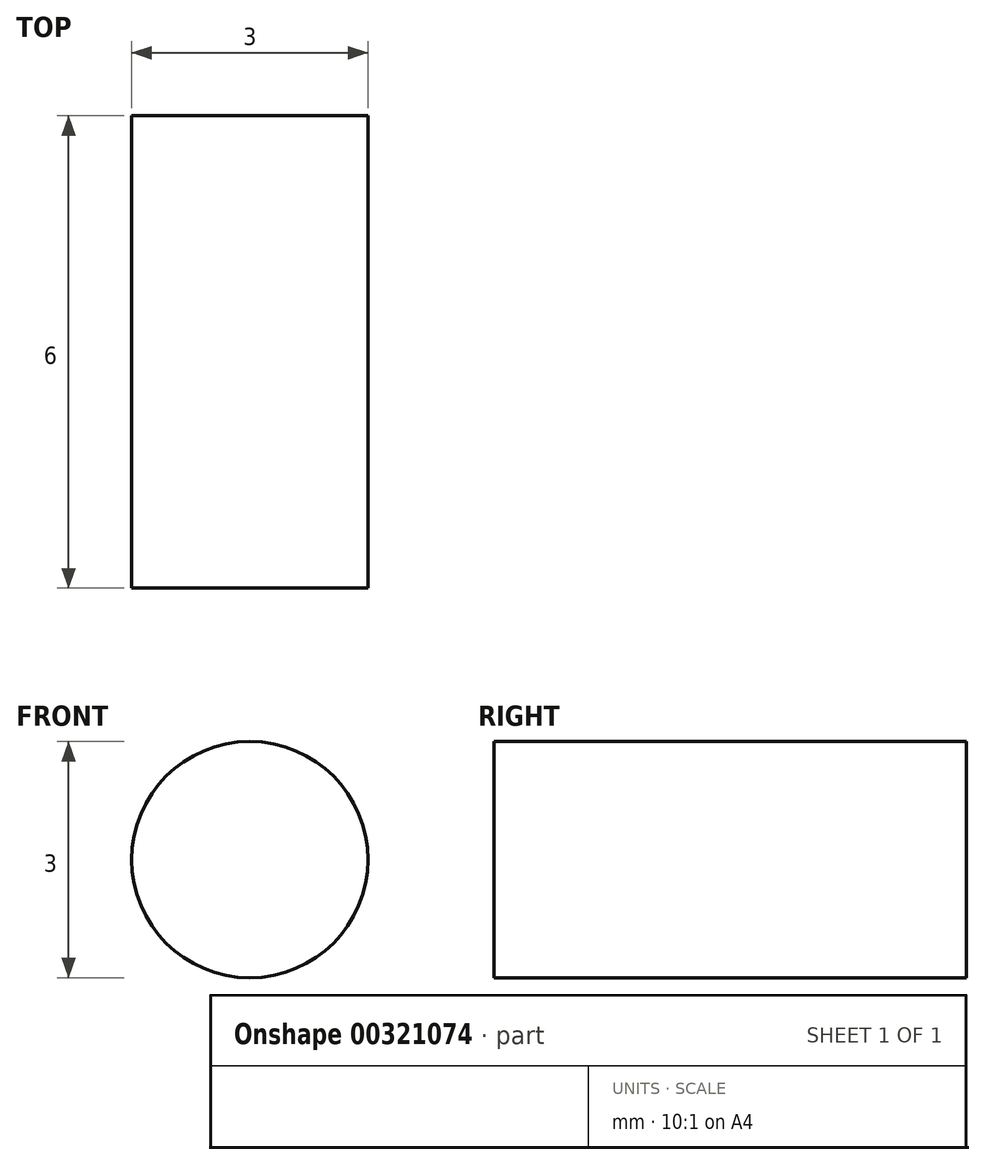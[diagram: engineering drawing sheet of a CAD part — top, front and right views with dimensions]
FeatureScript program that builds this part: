
annotation { "Feature Type Name" : "Feature", "Feature Type Description" : "" }
export const myFeature = defineFeature(function(context is Context, id is Id, definition is map)
    precondition{}
    {
        {
            var Q0;
            Q0=qCreatedBy(makeId("Front.planeOp"),FACE);
            var sketch = newSketch(context, id + "F0", { "sketchPlane" : qUnion([Q0])});
            skCircle(sketch, "E0", {"center": v(0, 0) * mm, "radius": 1.5 * mm});
            skSolve(sketch);
        }
        {
            var Q0;
            Q0 = qSketchRegion(id + "F0", true);
            extrude(context, id + "F1", {"entities" : qUnion([Q0]), "depth" : 6 * mm});
        }
    });
